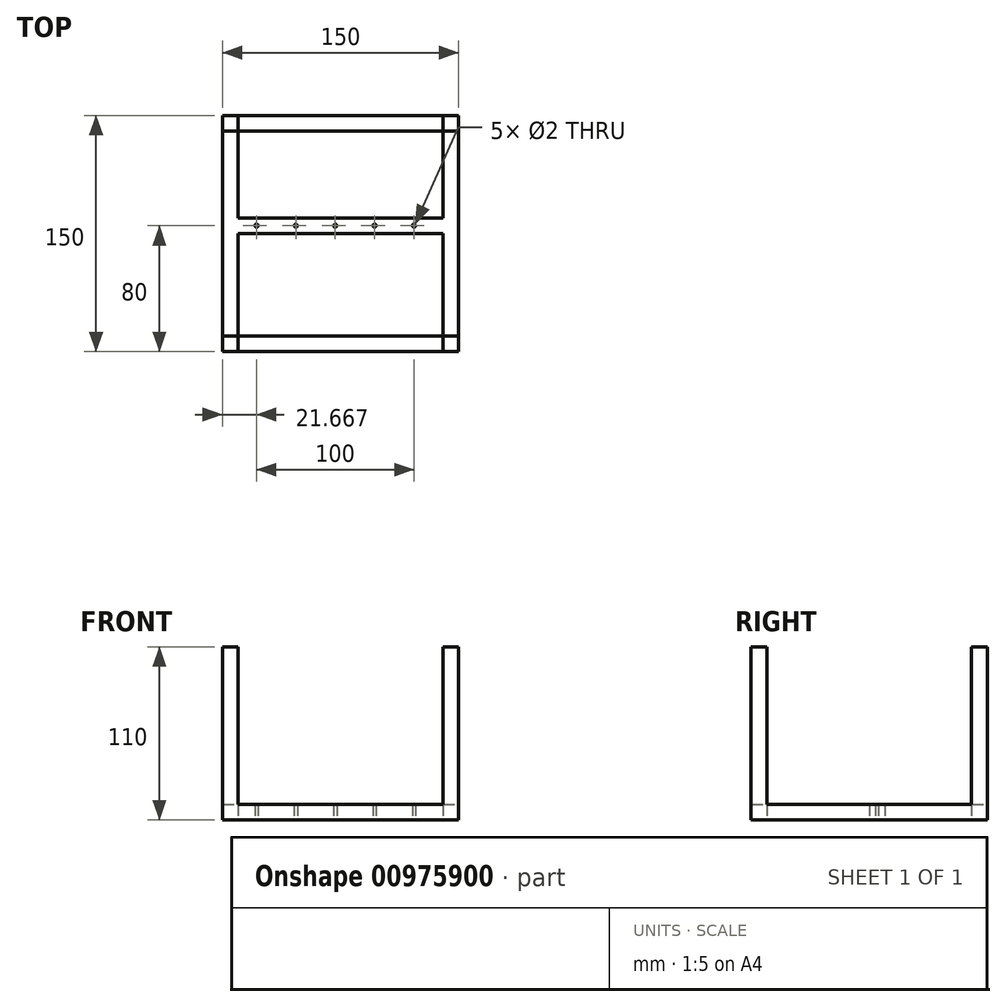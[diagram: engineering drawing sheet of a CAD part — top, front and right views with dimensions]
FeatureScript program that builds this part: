
annotation { "Feature Type Name" : "Feature", "Feature Type Description" : "" }
export const myFeature = defineFeature(function(context is Context, id is Id, definition is map)
    precondition{}
    {
        {
            var Q0;
            Q0=qCreatedBy(makeId("Top.planeOp"),FACE);
            var sketch = newSketch(context, id + "F0", { "sketchPlane" : qUnion([Q0])});
            skLineSegment(sketch, "E0.bottom", {"start": v(0, 0) * mm, "end": v(140, 0) * mm});
            skLineSegment(sketch, "E0.top", {"start": v(0, 10) * mm, "end": v(140, 10) * mm});
            skLineSegment(sketch, "E0.left", {"start": v(0, 0) * mm, "end": v(0, 10) * mm});
            skLineSegment(sketch, "E0.right", {"start": v(140, 0) * mm, "end": v(140, 10) * mm});
            skLineSegment(sketch, "E1.bottom", {"start": v(140, 0) * mm, "end": v(150, 0) * mm});
            skLineSegment(sketch, "E1.top", {"start": v(140, 150) * mm, "end": v(150, 150) * mm});
            skLineSegment(sketch, "E1.left", {"start": v(140, 0) * mm, "end": v(140, 150) * mm});
            skLineSegment(sketch, "E1.right", {"start": v(150, 0) * mm, "end": v(150, 150) * mm});
            skLineSegment(sketch, "E2.bottom", {"start": v(140, 150) * mm, "end": v(0, 150) * mm});
            skLineSegment(sketch, "E2.top", {"start": v(140, 140) * mm, "end": v(0, 140) * mm});
            skLineSegment(sketch, "E2.left", {"start": v(140, 150) * mm, "end": v(140, 140) * mm});
            skLineSegment(sketch, "E2.right", {"start": v(0, 150) * mm, "end": v(0, 140) * mm});
            skLineSegment(sketch, "E3.bottom", {"start": v(0, 140) * mm, "end": v(10, 140) * mm});
            skLineSegment(sketch, "E3.top", {"start": v(0, 10) * mm, "end": v(10, 10) * mm});
            skLineSegment(sketch, "E3.left", {"start": v(0, 140) * mm, "end": v(0, 10) * mm});
            skLineSegment(sketch, "E3.right", {"start": v(10, 140) * mm, "end": v(10, 10) * mm});
            skLineSegment(sketch, "E4.bottom", {"start": v(10, 85) * mm, "end": v(140, 85) * mm});
            skLineSegment(sketch, "E4.top", {"start": v(10, 75) * mm, "end": v(140, 75) * mm});
            skLineSegment(sketch, "E4.left", {"start": v(10, 85) * mm, "end": v(10, 75) * mm});
            skLineSegment(sketch, "E4.right", {"start": v(140, 85) * mm, "end": v(140, 75) * mm});
            skCircle(sketch, "E5", {"center": v(21.67, 80) * mm, "radius": 1 * mm});
            skCircle(sketch, "E6.1.0.0", {"center": v(46.67, 80) * mm, "radius": 1 * mm});
            skCircle(sketch, "E6.2.0.0", {"center": v(71.67, 80) * mm, "radius": 1 * mm});
            skCircle(sketch, "E6.3.0.0", {"center": v(96.67, 80) * mm, "radius": 1 * mm});
            skCircle(sketch, "E6.4.0.0", {"center": v(121.67, 80) * mm, "radius": 1 * mm});
            skLineSegment(sketch, "E6.direction1", {"start": v(21.67, 80) * mm, "end": v(46.67, 80) * mm, "construction": true});
            skSolve(sketch);
        }
        {
            var Q0;
            {var subQ0=sQuery(id+"F0.wireOp",EDGE,"E3.left");Q0=makeQuery(id+"F0.imprint","IMPRINT",FACE,{"disambiguationData":[TD([[makeQuery(id+"F0.imprint","IMPRINT",EDGE,{"derivedFrom":subQ0}),1.0]])]});}
            var Q1;
            {var subQ4=sQuery(id+"F0.wireOp",EDGE,"E2.bottom");Q1=makeQuery(id+"F0.imprint","IMPRINT",FACE,{"disambiguationData":[TD([[makeQuery(id+"F0.imprint","IMPRINT",EDGE,{"derivedFrom":subQ4}),1.0]])]});}
            var Q2;
            {var subQ1=sQuery(id+"F0.wireOp",EDGE,"E0.right");Q2=makeQuery(id+"F0.imprint","IMPRINT",FACE,{"disambiguationData":[TD([[makeQuery(id+"F0.imprint","IMPRINT",EDGE,{"derivedFrom":subQ1}),-1.0]])]});}
            var Q3;
            Q3=makeQuery(id+"F0.imprint","IMPRINT",FACE,{"disambiguationData":[TD([[makeQuery(id+"F0.imprint","IMPRINT",EDGE,{"derivedFrom":sQuery(id+"F0.wireOp",EDGE,"E0.bottom")}),1.0]])]});
            var Q4;
            {var subQ1=sQuery(id+"F0.wireOp",EDGE,"E4.bottom");Q4=makeQuery(id+"F0.imprint","IMPRINT",FACE,{"disambiguationData":[TD([[makeQuery(id+"F0.imprint","IMPRINT",EDGE,{"derivedFrom":subQ1}),-1.0]])]});}
            extrude(context, id + "F1", {"entities" : qUnion([Q0, Q1, Q2, Q3, Q4]), "depth" : 10 * mm, "offsetDistance" : 25 * mm});
        }
        {
            var Q0;
            Q0=makeQuery(id+"F1.opExtrude","CAP_FACE",FACE,{"disambiguationData":[OSD([sQuery(id+"F0.wireOp",EDGE,"E0.bottom"),sQuery(id+"F0.wireOp",EDGE,"E0.top"),sQuery(id+"F0.wireOp",EDGE,"E0.left"),sQuery(id+"F0.wireOp",EDGE,"E1.bottom"),sQuery(id+"F0.wireOp",EDGE,"E1.top"),sQuery(id+"F0.wireOp",EDGE,"E1.left"),sQuery(id+"F0.wireOp",EDGE,"E1.right"),sQuery(id+"F0.wireOp",EDGE,"E2.bottom"),sQuery(id+"F0.wireOp",EDGE,"E2.top"),sQuery(id+"F0.wireOp",EDGE,"E2.right"),sQuery(id+"F0.wireOp",EDGE,"E3.left"),sQuery(id+"F0.wireOp",EDGE,"E3.right"),sQuery(id+"F0.wireOp",EDGE,"E4.bottom"),sQuery(id+"F0.wireOp",EDGE,"E4.top"),sQuery(id+"F0.wireOp",EDGE,"E5"),sQuery(id+"F0.wireOp",EDGE,"E6.1.0.0"),sQuery(id+"F0.wireOp",EDGE,"E6.2.0.0"),sQuery(id+"F0.wireOp",EDGE,"E6.3.0.0"),sQuery(id+"F0.wireOp",EDGE,"E6.4.0.0")])],"isStart":false});
            var sketch = newSketch(context, id + "F2", { "sketchPlane" : qUnion([Q0])});
            skLineSegment(sketch, "E7.bottom", {"start": v(0, 150) * mm, "end": v(10, 150) * mm});
            skLineSegment(sketch, "E7.top", {"start": v(0, 140) * mm, "end": v(10, 140) * mm});
            skLineSegment(sketch, "E7.left", {"start": v(0, 150) * mm, "end": v(0, 140) * mm});
            skLineSegment(sketch, "E7.right", {"start": v(10, 150) * mm, "end": v(10, 140) * mm});
            skLineSegment(sketch, "E8.bottom", {"start": v(0, 0) * mm, "end": v(10, 0) * mm});
            skLineSegment(sketch, "E8.top", {"start": v(0, 10) * mm, "end": v(10, 10) * mm});
            skLineSegment(sketch, "E8.left", {"start": v(0, 0) * mm, "end": v(0, 10) * mm});
            skLineSegment(sketch, "E8.right", {"start": v(10, 0) * mm, "end": v(10, 10) * mm});
            skLineSegment(sketch, "E9.bottom", {"start": v(150, 0) * mm, "end": v(140, 0) * mm});
            skLineSegment(sketch, "E9.top", {"start": v(150, 10) * mm, "end": v(140, 10) * mm});
            skLineSegment(sketch, "E9.left", {"start": v(150, 0) * mm, "end": v(150, 10) * mm});
            skLineSegment(sketch, "E9.right", {"start": v(140, 0) * mm, "end": v(140, 10) * mm});
            skLineSegment(sketch, "E10.bottom", {"start": v(140, 140) * mm, "end": v(150, 140) * mm});
            skLineSegment(sketch, "E10.top", {"start": v(140, 150) * mm, "end": v(150, 150) * mm});
            skLineSegment(sketch, "E10.left", {"start": v(140, 140) * mm, "end": v(140, 150) * mm});
            skLineSegment(sketch, "E10.right", {"start": v(150, 140) * mm, "end": v(150, 150) * mm});
            skSolve(sketch);
        }
        {
            var Q0;
            Q0 = qSketchRegion(id + "F2", true);
            extrude(context, id + "F3", {"entities" : qUnion([Q0]), "operationType" : NewBodyOperationType.ADD, "depth" : 100 * mm, "offsetDistance" : 25 * mm});
        }
    });
